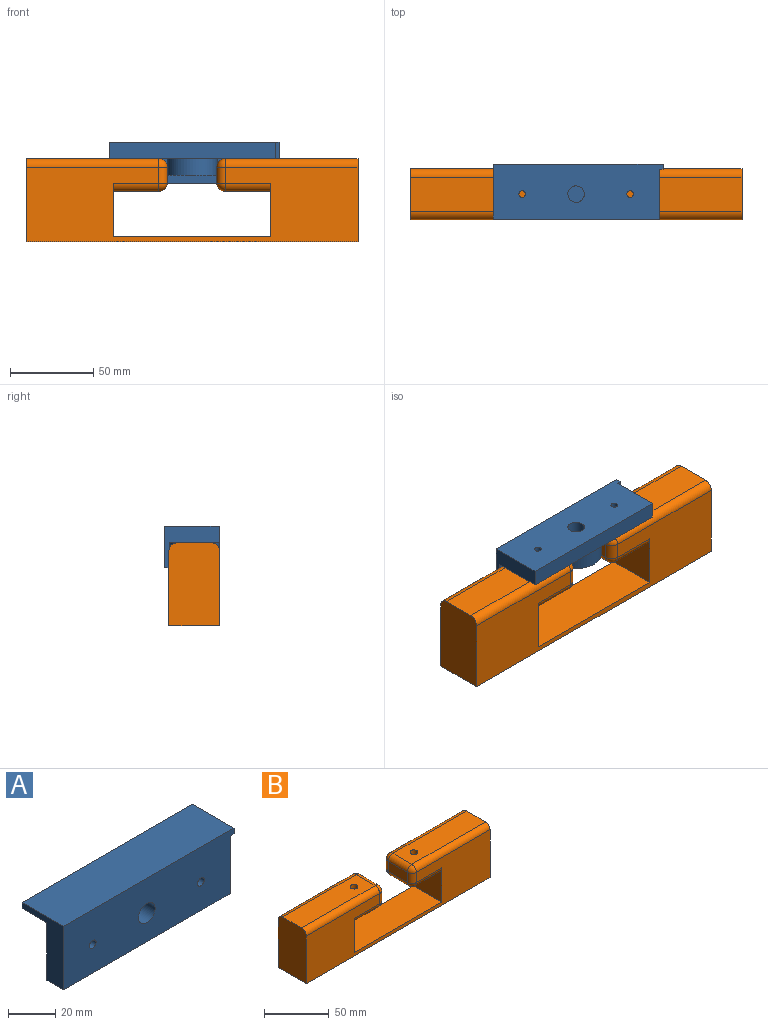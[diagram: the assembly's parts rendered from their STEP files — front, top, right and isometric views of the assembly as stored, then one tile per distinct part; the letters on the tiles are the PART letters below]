
ASSEMBLY  parts=2 mates=1
PART A: 15 faces, bbox 102.4x25x33 mm
  f0: plane 102.4x33mm, normal (0,-1,0), area 3203.5mm2, adj f2,f3,f4,f5,f6,f7,f9,f10
  f1: plane 100x30mm, normal (0,1,0), area 2268.5mm2, adj f2,f3,f4,f6,f7,f11,f13
  f2: plane 33x25mm, normal (-1,0,0), area 375mm2, adj f0,f1,f3,f8,f10,f11
  f3: plane 100x10mm, normal (0,0,-1), area 1000mm2, adj f0,f1,f2,f4
  f4: plane 30x10mm, normal (1,0,0), area 300mm2, adj f0,f1,f3,f11
  f5: cylinder r=5mm len=10mm, axis (0,-1,0), area 314.2mm2, adj f0,f14
  f6: cylinder r=2mm len=10mm, axis (0,-1,0), area 125.7mm2, adj f0,f1
  f7: cylinder r=2mm len=10mm, axis (0,-1,0), area 125.7mm2, adj f0,f1
  f8: plane 102.4x3mm, normal (0,1,0), area 307.2mm2, adj f2,f9,f10,f11
  f9: plane 25x3mm, normal (1,0,0), area 75mm2, adj f0,f8,f10,f11
  f10: plane 102.4x25mm, normal (0,0,1), area 2560mm2, adj f0,f2,f8,f9
  f11: plane 102.4x25mm, normal (0,0,-1), area 1560mm2, adj f0,f1,f2,f4,f8,f9
  f12: plane 29.99x29.99mm, normal (0,1,0), area 706.4mm2, adj f13
  f13: cylinder r=14.99mm len=29.99mm, axis (0,-1,0), area 942.2mm2, adj f1,f12
  f14: plane 10x10mm, normal (0,-1,0), area 78.5mm2, adj f5
PART B: 40 faces, bbox 200x30.7x50 mm
  f0: plane 80x20.65mm, normal (0,0,1), area 1623.7mm2, adj f11,f25,f27,f28,f39
  f1: plane 20.65x9.65mm, normal (-1,0,0), area 199.3mm2, adj f21,f24,f27,f30
  f2: plane 27.5x20.65mm, normal (0,0,-1), area 539.6mm2, adj f3,f22,f24,f32,f39
  f3: plane 32.17x30.65mm, normal (-1,0,0), area 843.6mm2, adj f2,f4,f12,f13,f22,f32
  f4: plane 95x30.65mm, normal (0,0,1), area 2911.8mm2, adj f3,f5,f12,f13
  f5: plane 32.17x30.65mm, normal (1,0,0), area 843.6mm2, adj f4,f6,f12,f13,f18,f33
  f6: plane 27.5x20.65mm, normal (0,0,-1), area 539.6mm2, adj f5,f18,f20,f33,f38
  f7: plane 20.65x9.65mm, normal (1,0,0), area 199.3mm2, adj f15,f17,f20,f35
  f8: plane 80x20.65mm, normal (0,0,1), area 1623.7mm2, adj f9,f14,f17,f37,f38
  f9: plane 50x30.65mm, normal (-1,0,0), area 1521.8mm2, adj f8,f10,f12,f13,f14,f37
  f10: plane 200x30.65mm, normal (0,0,-1), area 6130mm2, adj f9,f11,f12,f13
  f11: plane 50x30.65mm, normal (1,0,0), area 1521.8mm2, adj f0,f10,f12,f13,f25,f28
  f12: plane 200x45mm, normal (0,-1,0), area 5557.6mm2, adj f3,f4,f5,f9,f10,f11,f14,f15
  f13: plane 200x45mm, normal (0,1,0), area 5557.6mm2, adj f3,f4,f5,f9,f10,f11,f28,f30
  f14: cylinder r=5mm len=80mm, axis (1,0,0), area 628.3mm2, adj f8,f9,f12,f16
  f15: cylinder r=5mm len=9.65mm, axis (0,0,-1), area 75.8mm2, adj f7,f12,f16,f19
  f16: sphere r=5mm, area 39.3mm2, adj f14,f15,f17
  f17: cylinder r=5mm len=20.65mm, axis (0,1,0), area 162.2mm2, adj f7,f8,f16,f36
  f18: cylinder r=5mm len=27.5mm, axis (-1,0,0), area 216mm2, adj f5,f6,f12,f19
  f19: sphere r=5mm, area 39.3mm2, adj f15,f18,f20
  f20: cylinder r=5mm len=20.65mm, axis (0,-1,0), area 162.2mm2, adj f6,f7,f19,f34
  f21: cylinder r=5mm len=9.65mm, axis (0,0,1), area 75.8mm2, adj f1,f12,f23,f26
  f22: cylinder r=5mm len=27.5mm, axis (-1,0,0), area 216mm2, adj f2,f3,f12,f23
  f23: sphere r=5mm, area 39.3mm2, adj f21,f22,f24
  f24: cylinder r=5mm len=20.65mm, axis (0,-1,0), area 162.2mm2, adj f1,f2,f23,f31
  f25: cylinder r=5mm len=80mm, axis (1,0,0), area 628.3mm2, adj f0,f11,f12,f26
  f26: sphere r=5mm, area 39.3mm2, adj f21,f25,f27
  f27: cylinder r=5mm len=20.65mm, axis (0,-1,0), area 162.2mm2, adj f0,f1,f26,f29
  f28: cylinder r=5mm len=80mm, axis (-1,0,0), area 628.3mm2, adj f0,f11,f13,f29
  f29: sphere r=5mm, area 39.3mm2, adj f27,f28,f30
  f30: cylinder r=5mm len=9.65mm, axis (0,0,-1), area 75.8mm2, adj f1,f13,f29,f31
  f31: sphere r=5mm, area 39.3mm2, adj f24,f30,f32
  f32: cylinder r=5mm len=27.5mm, axis (1,0,0), area 216mm2, adj f2,f3,f13,f31
  f33: cylinder r=5mm len=27.5mm, axis (1,0,0), area 216mm2, adj f5,f6,f13,f34
  f34: sphere r=5mm, area 39.3mm2, adj f20,f33,f35
  f35: cylinder r=5mm len=9.65mm, axis (0,0,1), area 75.8mm2, adj f7,f13,f34,f36
  f36: sphere r=5mm, area 39.3mm2, adj f17,f35,f37
  f37: cylinder r=5mm len=80mm, axis (-1,0,0), area 628.3mm2, adj f8,f9,f13,f36
  f38: cylinder r=3mm len=19.65mm, axis (0,0,1), area 370.4mm2, adj f6,f8
  f39: cylinder r=3mm len=19.65mm, axis (0,0,1), area 370.4mm2, adj f0,f2
PLACE A rot(axis=(-1,0,0),90deg) t=(-1.9,-13.36,6.7)mm
PLACE B t=(-2,1.97,-18.3)mm
MATE planar A.f6 <-> B.f39  axis (0,0,-1) through (30.6,-13.36,6.7)mm
